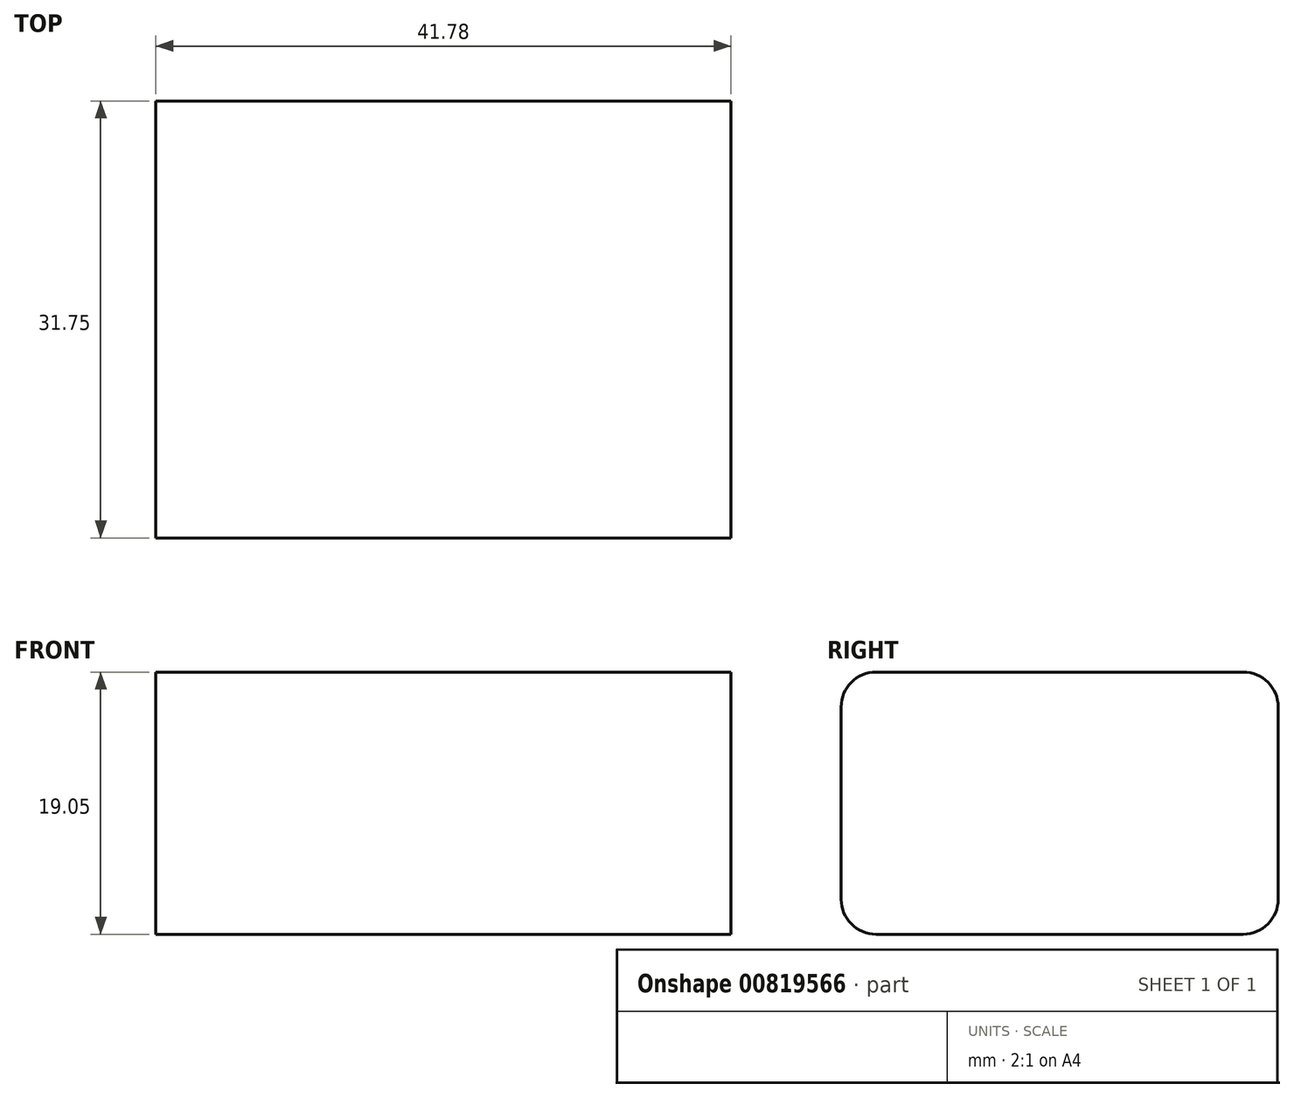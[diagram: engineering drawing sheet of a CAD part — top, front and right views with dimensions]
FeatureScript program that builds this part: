
annotation { "Feature Type Name" : "Feature", "Feature Type Description" : "" }
export const myFeature = defineFeature(function(context is Context, id is Id, definition is map)
    precondition{}
    {
        {
            var Q0;
            Q0=qCreatedBy(makeId("Top.planeOp"),FACE);
            var sketch = newSketch(context, id + "F0", { "sketchPlane" : qUnion([Q0])});
            skLineSegment(sketch, "E0.bottom", {"start": v(-19.17, 11.45) * mm, "end": v(22.6, 11.45) * mm});
            skLineSegment(sketch, "E0.top", {"start": v(-19.17, -20.3) * mm, "end": v(22.6, -20.3) * mm});
            skLineSegment(sketch, "E0.left", {"start": v(-19.17, 11.45) * mm, "end": v(-19.17, -20.3) * mm});
            skLineSegment(sketch, "E0.right", {"start": v(22.6, 11.45) * mm, "end": v(22.6, -20.3) * mm});
            skSolve(sketch);
        }
        {
            var Q0;
            Q0 = qSketchRegion(id + "F0", true);
            extrude(context, id + "F1", {"entities" : qUnion([Q0]), "depth" : 19.05 * mm, "offsetDistance" : 25.4 * mm});
        }
        {
            var Q0;
            Q0=makeQuery(id+"F1.opExtrude","CAP_EDGE",EDGE,{"disambiguationData":[OSD([sQuery(id+"F0.wireOp",EDGE,"E0.bottom")])],"isStart":false});
            var Q1;
            Q1=makeQuery(id+"F1.opExtrude","CAP_EDGE",EDGE,{"disambiguationData":[OSD([sQuery(id+"F0.wireOp",EDGE,"E0.bottom")])],"isStart":true});
            var Q2;
            Q2=makeQuery(id+"F1.opExtrude","CAP_EDGE",EDGE,{"disambiguationData":[OSD([sQuery(id+"F0.wireOp",EDGE,"E0.top")])],"isStart":false});
            var Q3;
            Q3=makeQuery(id+"F1.opExtrude","CAP_EDGE",EDGE,{"disambiguationData":[OSD([sQuery(id+"F0.wireOp",EDGE,"E0.top")])],"isStart":true});
            fillet(context, id + "F2", {"entities" : qUnion([Q0, Q1, Q2, Q3]), "radius" : 2.54 * mm, "tangentPropagation" : true, "allowEdgeOverflow" : false});
        }
    });
